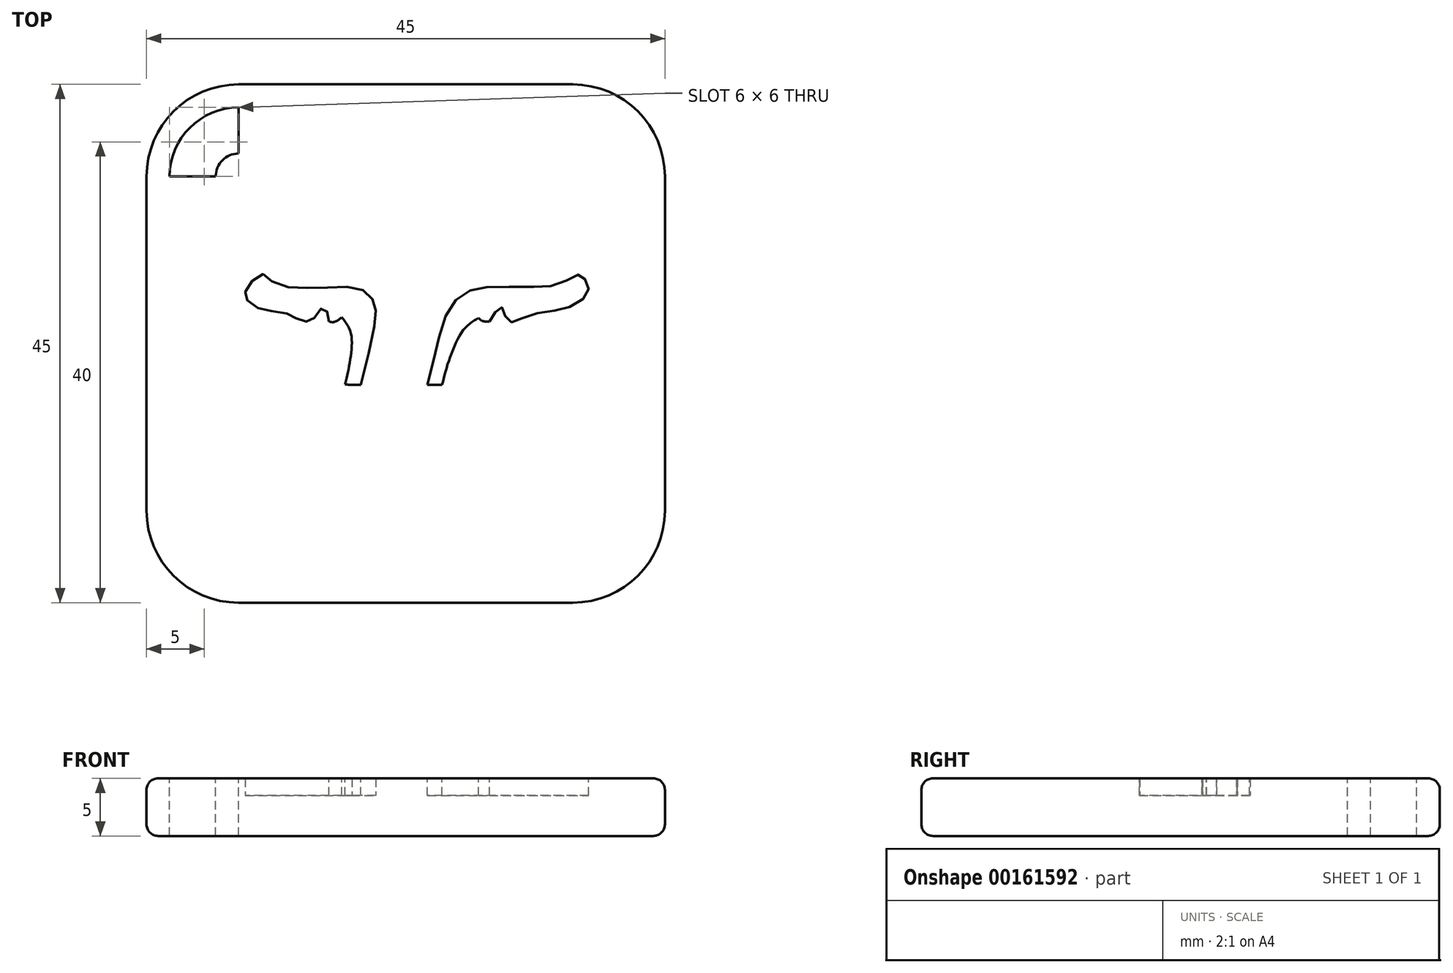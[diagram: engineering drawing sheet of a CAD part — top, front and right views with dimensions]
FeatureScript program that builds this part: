
annotation { "Feature Type Name" : "Feature", "Feature Type Description" : "" }
export const myFeature = defineFeature(function(context is Context, id is Id, definition is map)
    precondition{}
    {
        {
            var Q0;
            Q0=qCreatedBy(makeId("Top.planeOp"),FACE);
            var sketch = newSketch(context, id + "F0", { "sketchPlane" : qUnion([Q0])});
            skLineSegment(sketch, "E0.bottom", {"start": v(-22.5, 22.5) * mm, "end": v(22.5, 22.5) * mm});
            skLineSegment(sketch, "E0.top", {"start": v(-22.5, -22.5) * mm, "end": v(22.5, -22.5) * mm});
            skLineSegment(sketch, "E0.left", {"start": v(-22.5, 22.5) * mm, "end": v(-22.5, -22.5) * mm});
            skLineSegment(sketch, "E0.right", {"start": v(22.5, 22.5) * mm, "end": v(22.5, -22.5) * mm});
            skPoint(sketch, "E1", {"position": v(0, 22.5) * mm});
            skPoint(sketch, "E2", {"position": v(22.5, 0) * mm});
            skSolve(sketch);
        }
        {
            var Q0;
            Q0=qSketchRegion(id+"F0",true);
            extrude(context, id + "F1", {"entities" : qUnion([Q0]), "depth" : 5 * mm});
        }
        {
            var Q0;
            Q0=makeQuery(id+"F1.opExtrude","CAP_FACE",FACE,{"disambiguationData":[OSD([sQuery(id+"F0.wireOp",EDGE,"E0.bottom"),sQuery(id+"F0.wireOp",EDGE,"E0.top"),sQuery(id+"F0.wireOp",EDGE,"E0.left"),sQuery(id+"F0.wireOp",EDGE,"E0.right")])],"isStart":false});
            var sketch = newSketch(context, id + "F2", { "sketchPlane" : qUnion([Q0])});
            skPoint(sketch, "E3", {"position": v(0, 19.42) * mm});
            skPoint(sketch, "E4", {"position": v(22.5, 0) * mm});
            skPoint(sketch, "E5", {"position": v(0, 22.5) * mm});
            skFitSpline(sketch, "E6", {"points": [v(-10.99, 17.96) * mm, v(-6.67, 16.95) * mm, v(-3.8, 15.5) * mm, v(-1.73, 13.83) * mm], "startDerivative": vector(12.1, -2.63) * mm, "endDerivative": vector(7.1, -5.95) * mm});
            skFitSpline(sketch, "E7", {"points": [v(-1.73, 13.83) * mm, v(1.93, 14.01) * mm, v(5.49, 13.96) * mm, v(8.15, 13.83) * mm], "startDerivative": vector(10.33, 0.9) * mm, "endDerivative": vector(8.55, -0.72) * mm});
            skFitSpline(sketch, "E8", {"points": [v(8.15, 13.83) * mm, v(9.82, 14.8) * mm, v(13.73, 16.7) * mm, v(19.48, 18.03) * mm], "startDerivative": vector(6.27, 4) * mm, "endDerivative": vector(14.4, 2.4) * mm});
            skFitSpline(sketch, "E9", {"points": [v(19.48, 18.03) * mm, v(19.95, 16.98) * mm, v(20.58, 14.3) * mm, v(20.04, 11.7) * mm, v(19.14, 9.8) * mm, v(17.57, 7.66) * mm, v(17.57, 7.66) * mm], "startDerivative": vector(3.43, -6.2) * mm, "endDerivative": vector(-0.62, 0.45) * mm});
            skFitSpline(sketch, "E10", {"points": [v(17.57, 7.66) * mm, v(18.66, 6.83) * mm, v(19.79, 5.6) * mm, v(21, 3.47) * mm, v(21.02, 1.64) * mm, v(20.45, -0.51) * mm, v(19.02, -3.1) * mm], "startDerivative": vector(7.54, -6.14) * mm, "endDerivative": vector(-8.05, -12.97) * mm});
            skFitSpline(sketch, "E11", {"points": [v(19.02, -3.1) * mm, v(18.46, -2.57) * mm, v(17.94, -2.35) * mm], "startDerivative": vector(-1.02, 1.1) * mm, "endDerivative": vector(-1.13, 0.4) * mm});
            skFitSpline(sketch, "E12", {"points": [v(17.94, -2.35) * mm, v(17.32, -3.93) * mm, v(16.2, -5.3) * mm, v(15.51, -5.8) * mm], "startDerivative": vector(-1.51, -4.58) * mm, "endDerivative": vector(-1.47, -1.77) * mm});
            skFitSpline(sketch, "E13", {"points": [v(15.51, -5.8) * mm, v(15.34, -4.95) * mm, v(14.8, -4.37) * mm], "startDerivative": vector(-0.01, 1.8) * mm, "endDerivative": vector(-0.19, 0.23) * mm});
            skFitSpline(sketch, "E14", {"points": [v(14.8, -4.37) * mm, v(14.55, -4.88) * mm, v(13.51, -6.28) * mm, v(12.21, -7.43) * mm, v(11.26, -7.78) * mm], "startDerivative": vector(-1.12, -2.62) * mm, "endDerivative": vector(-4.09, -1.1) * mm});
            skFitSpline(sketch, "E15", {"points": [v(11.26, -7.78) * mm, v(11.11, -6.74) * mm, v(10.42, -5.88) * mm], "startDerivative": vector(-0.05, 2.2) * mm, "endDerivative": vector(-1.63, 1.67) * mm});
            skFitSpline(sketch, "E16", {"points": [v(10.42, -5.88) * mm, v(10.03, -6.36) * mm, v(8.14, -8.14) * mm, v(6.66, -8.75) * mm], "startDerivative": vector(-1.32, -1.92) * mm, "endDerivative": vector(-4.03, -1) * mm});
            skFitSpline(sketch, "E17", {"points": [v(6.66, -8.75) * mm, v(6.66, -7.96) * mm, v(6.49, -7.01) * mm, v(6.05, -6.24) * mm, v(5.88, -6.12) * mm], "startDerivative": vector(0.1, 2.83) * mm, "endDerivative": vector(-1.15, 0.55) * mm});
            skFitSpline(sketch, "E18", {"points": [v(5.88, -6.12) * mm, v(5.27, -6.68) * mm, v(2.3, -11.05) * mm, v(-0.84, -15.23) * mm, v(-3.18, -17.45) * mm, v(-4.52, -17.94) * mm, v(-5.68, -17.34) * mm, v(-6.99, -14.65) * mm, v(-8.74, -7.01) * mm, v(-9.06, -6.15) * mm], "startDerivative": vector(-8.59, -6.54) * mm, "endDerivative": vector(-4.62, 9.1) * mm});
            skFitSpline(sketch, "E19", {"points": [v(-9.06, -6.15) * mm, v(-9.62, -6.41) * mm, v(-10.7, -7.74) * mm, v(-11.17, -8.83) * mm], "startDerivative": vector(-2.18, -0.85) * mm, "endDerivative": vector(-0.22, -0.54) * mm});
            skFitSpline(sketch, "E20", {"points": [v(-11.17, -8.83) * mm, v(-11.66, -8.51) * mm, v(-12.52, -7.94) * mm, v(-13.28, -6.72) * mm, v(-13.5, -5.86) * mm], "startDerivative": vector(-2.33, 1.17) * mm, "endDerivative": vector(-0.64, 3.34) * mm});
            skFitSpline(sketch, "E21", {"points": [v(-13.5, -5.86) * mm, v(-14.15, -6.26) * mm, v(-15.03, -7.37) * mm, v(-15.3, -7.76) * mm], "startDerivative": vector(-1.95, -0.91) * mm, "endDerivative": vector(-0.85, -1.3) * mm});
            skFitSpline(sketch, "E22", {"points": [v(-15.3, -7.76) * mm, v(-15.84, -7.58) * mm, v(-16.47, -7.03) * mm, v(-16.9, -6.04) * mm, v(-17.12, -5.3) * mm, v(-17.21, -4.47) * mm], "startDerivative": vector(-3.23, 0.77) * mm, "endDerivative": vector(-0.32, 4.26) * mm});
            skFitSpline(sketch, "E23", {"points": [v(-17.21, -4.47) * mm, v(-17.79, -4.83) * mm, v(-18.39, -5.5) * mm, v(-18.57, -5.76) * mm], "startDerivative": vector(-1.6, -0.83) * mm, "endDerivative": vector(-0.61, -0.95) * mm});
            skFitSpline(sketch, "E24", {"points": [v(-18.57, -5.76) * mm, v(-18.91, -5.4) * mm, v(-19.37, -4.63) * mm, v(-19.48, -3.72) * mm, v(-19.42, -2.9) * mm, v(-19.34, -2.33) * mm], "startDerivative": vector(-1.95, 2) * mm, "endDerivative": vector(0.47, 3.1) * mm});
            skFitSpline(sketch, "E25", {"points": [v(-19.34, -2.33) * mm, v(-19.79, -2.53) * mm, v(-20.83, -3) * mm], "startDerivative": vector(-1.04, -0.42) * mm, "endDerivative": vector(-1.81, -1.1) * mm});
            skFitSpline(sketch, "E26", {"points": [v(-20.83, -3) * mm, v(-21, -1.25) * mm, v(-19.6, 3.43) * mm, v(-14.29, 7.66) * mm], "startDerivative": vector(-1.5, 7.35) * mm, "endDerivative": vector(14.98, 8.8) * mm});
            skFitSpline(sketch, "E27", {"points": [v(-14.29, 7.66) * mm, v(-14.63, 9.8) * mm, v(-14.46, 12.44) * mm, v(-13.34, 15.3) * mm, v(-10.99, 17.96) * mm], "startDerivative": vector(-2.7, 9.33) * mm, "endDerivative": vector(8.61, 9.84) * mm});
            skFitSpline(sketch, "E28", {"points": [v(-11.82, 7.22) * mm, v(-12.36, 11.13) * mm, v(-11.43, 14.91) * mm, v(-10.34, 16.17) * mm], "startDerivative": vector(-2.56, 9.75) * mm, "endDerivative": vector(4.88, 4.44) * mm});
            skFitSpline(sketch, "E29", {"points": [v(-10.34, 16.17) * mm, v(-6.96, 15.19) * mm, v(-4.57, 13.4) * mm, v(-2.66, 11.86) * mm], "startDerivative": vector(9.47, -2.48) * mm, "endDerivative": vector(5.95, -4.79) * mm});
            skFitSpline(sketch, "E30", {"points": [v(-2.66, 11.86) * mm, v(-0.71, 12) * mm, v(1.24, 12.12) * mm, v(5.72, 12.04) * mm, v(8.17, 11.86) * mm], "startDerivative": vector(9.3, 1.33) * mm, "endDerivative": vector(8.98, -1.39) * mm});
            skFitSpline(sketch, "E31", {"points": [v(8.17, 11.86) * mm, v(11.95, 14.03) * mm, v(16.86, 16.09) * mm, v(17.95, 16.22) * mm], "startDerivative": vector(9.23, 6) * mm, "endDerivative": vector(5.74, 0.8) * mm});
            skFitSpline(sketch, "E32", {"points": [v(17.95, 16.22) * mm, v(18.34, 15.3) * mm, v(18.46, 13.86) * mm, v(17.71, 11.66) * mm, v(15.1, 7.33) * mm], "startDerivative": vector(2.53, -5.22) * mm, "endDerivative": vector(-7.95, -12.35) * mm});
            skFitSpline(sketch, "E33", {"points": [v(15.1, 7.33) * mm, v(16.28, 6.28) * mm, v(17.98, 4.2) * mm, v(18.58, 1.32) * mm, v(18.17, -0.47) * mm], "startDerivative": vector(5.27, -4.55) * mm, "endDerivative": vector(-2.46, -7.24) * mm});
            skFitSpline(sketch, "E34", {"points": [v(18.17, -0.47) * mm, v(16.95, -0.28) * mm, v(15.74, -2.26) * mm], "startDerivative": vector(-3.13, 1.27) * mm, "endDerivative": vector(-1.85, -4.58) * mm});
            skFitSpline(sketch, "E35", {"points": [v(15.74, -2.26) * mm, v(14.32, -2.15) * mm, v(13.59, -2.49) * mm, v(12.9, -3.53) * mm, v(12.5, -4.63) * mm], "startDerivative": vector(-5.57, 0.88) * mm, "endDerivative": vector(-1.39, -4.3) * mm});
            skFitSpline(sketch, "E36", {"points": [v(12.5, -4.63) * mm, v(11.93, -3.83) * mm, v(10.85, -3.58) * mm, v(9.81, -4.1) * mm, v(8.35, -5.47) * mm], "startDerivative": vector(-2.05, 4.14) * mm, "endDerivative": vector(-4.82, -4.89) * mm});
            skFitSpline(sketch, "E37", {"points": [v(8.35, -5.47) * mm, v(7.95, -4.7) * mm, v(7.25, -3.94) * mm, v(6.42, -3.66) * mm, v(5.29, -3.83) * mm, v(4, -4.56) * mm, v(3.16, -5.88) * mm, v(1.27, -8.94) * mm, v(-1.32, -12.8) * mm, v(-3.03, -15.03) * mm, v(-3.77, -15.73) * mm, v(-3.98, -15.77) * mm, v(-4.3, -15.47) * mm, v(-4.8, -13.94) * mm, v(-5.58, -10.32) * mm, v(-6.04, -7.02) * mm, v(-6.35, -4.77) * mm, v(-6.82, -4.04) * mm, v(-7.86, -3.7) * mm, v(-8.72, -3.71) * mm, v(-9.28, -3.93) * mm, v(-10.11, -4.4) * mm, v(-11.18, -5.47) * mm], "startDerivative": vector(-10.14, 22.02) * mm, "endDerivative": vector(-23.4, -25.47) * mm});
            skFitSpline(sketch, "E38", {"points": [v(-11.18, -5.47) * mm, v(-11.68, -4.42) * mm, v(-12.64, -3.6) * mm, v(-13.9, -3.83) * mm, v(-15.05, -4.75) * mm], "startDerivative": vector(-1.65, 4.4) * mm, "endDerivative": vector(-3.87, -3.5) * mm});
            skFitSpline(sketch, "E39", {"points": [v(-15.05, -4.75) * mm, v(-14.87, -3.44) * mm, v(-15.11, -2.36) * mm, v(-16.79, -2.2) * mm, v(-17.15, -2.32) * mm], "startDerivative": vector(0.33, 4.33) * mm, "endDerivative": vector(-1.67, -0.76) * mm});
            skFitSpline(sketch, "E40", {"points": [v(-17.15, -2.32) * mm, v(-17.1, -1.32) * mm, v(-17.21, -0.43) * mm, v(-18.6, -0.43) * mm], "startDerivative": vector(0.04, 3) * mm, "endDerivative": vector(-4.65, -0.92) * mm});
            skFitSpline(sketch, "E41", {"points": [v(-18.6, -0.43) * mm, v(-17.48, 2.56) * mm, v(-14.24, 5.72) * mm, v(-11.82, 7.22) * mm], "startDerivative": vector(2.26, 9.56) * mm, "endDerivative": vector(7.62, 4.87) * mm});
            skFitSpline(sketch, "E42", {"points": [v(-3.9, -3.58) * mm, v(-5.25, -3.56) * mm], "startDerivative": vector(-2.2, -0.06) * mm, "endDerivative": vector(-0.4, -0.03) * mm});
            skFitSpline(sketch, "E43", {"points": [v(-5.25, -3.56) * mm, v(-4.8, -1.32) * mm, v(-4.78, 0.95) * mm, v(-5.54, 2.28) * mm], "startDerivative": vector(1.38, 6.15) * mm, "endDerivative": vector(-3.2, 4.1) * mm});
            skFitSpline(sketch, "E44", {"points": [v(-5.54, 2.28) * mm, v(-6.24, 1.87) * mm, v(-6.65, 1.91) * mm], "startDerivative": vector(-1.27, -0.93) * mm, "endDerivative": vector(-0.93, 0.27) * mm});
            skFitSpline(sketch, "E45", {"points": [v(-6.65, 1.91) * mm, v(-6.77, 2.6) * mm, v(-7, 3.06) * mm, v(-7.38, 3) * mm, v(-7.9, 2.25) * mm, v(-8.3, 1.95) * mm, v(-8.98, 1.95) * mm, v(-9.73, 2.32) * mm, v(-10.35, 2.61) * mm, v(-12.05, 2.87) * mm, v(-13.04, 3.2) * mm, v(-13.83, 3.89) * mm, v(-13.94, 4.34) * mm, v(-13.7, 5) * mm, v(-12.5, 6.03) * mm, v(-12.24, 5.91) * mm, v(-11.08, 5.11) * mm, v(-8.85, 4.83) * mm, v(-6.2, 4.9) * mm, v(-4.05, 4.8) * mm, v(-3, 4.05) * mm, v(-2.64, 3.17) * mm, v(-2.67, 1.87) * mm, v(-3.9, -3.58) * mm], "startDerivative": vector(-3.06, 20.2) * mm, "endDerivative": vector(-16.31, -66) * mm});
            skFitSpline(sketch, "E46", {"points": [v(1.89, -3.57) * mm, v(3.16, -3.59) * mm], "startDerivative": vector(1.31, -0.04) * mm, "endDerivative": vector(1.31, -0.04) * mm});
            skFitSpline(sketch, "E47", {"points": [v(3.16, -3.59) * mm, v(3.87, -1.13) * mm, v(5.14, 1.33) * mm, v(6.31, 2.22) * mm], "startDerivative": vector(1.57, 6.66) * mm, "endDerivative": vector(4.3, 2.6) * mm});
            skFitSpline(sketch, "E48", {"points": [v(6.31, 2.22) * mm, v(6.7, 1.95) * mm, v(7.26, 1.91) * mm], "startDerivative": vector(0.78, -0.73) * mm, "endDerivative": vector(0.04, 0) * mm});
            skFitSpline(sketch, "E49", {"points": [v(7.26, 1.91) * mm, v(7.72, 2.67) * mm, v(8.08, 3.08) * mm, v(8.43, 3.1) * mm, v(8.62, 2.43) * mm, v(8.96, 1.92) * mm, v(9.55, 1.92) * mm, v(10.74, 2.48) * mm, v(12.79, 2.84) * mm, v(14.39, 3.25) * mm, v(15.67, 4.16) * mm, v(15.87, 4.85) * mm, v(15.6, 5.54) * mm, v(15.11, 5.98) * mm, v(14.78, 5.9) * mm, v(13.15, 5.13) * mm, v(11.5, 4.91) * mm, v(7.66, 4.9) * mm, v(5.54, 4.58) * mm, v(3.92, 3.28) * mm, v(2.87, 0.42) * mm, v(1.89, -3.57) * mm], "startDerivative": vector(12.23, 20.39) * mm, "endDerivative": vector(-12.15, -48.42) * mm});
            skSolve(sketch);
        }
        {
            var Q0;
            Q0=makeQuery(id+"F2.imprint","IMPRINT",FACE,{"disambiguationData":[TD([[makeQuery(id+"F2.imprint","IMPRINT",EDGE,{"derivedFrom":sQuery(id+"F2.wireOp",EDGE,"E6")}),-1.0]])]});
            var Q1;
            Q1=makeQuery(id+"F2.imprint","IMPRINT",FACE,{"disambiguationData":[TD([[makeQuery(id+"F2.imprint","IMPRINT",EDGE,{"derivedFrom":sQuery(id+"F2.wireOp",EDGE,"E42")}),-1.0]])]});
            var Q2;
            Q2=makeQuery(id+"F2.imprint","IMPRINT",FACE,{"disambiguationData":[TD([[makeQuery(id+"F2.imprint","IMPRINT",EDGE,{"derivedFrom":sQuery(id+"F2.wireOp",EDGE,"E46")}),1.0]])]});
            extrude(context, id + "F3", {"entities" : qUnion([Q0, Q1, Q2]), "operationType" : NewBodyOperationType.REMOVE, "oppositeDirection" : true, "depth" : 1.5 * mm});
        }
        {
            var Q0;
            Q0=makeQuery(id+"F1.opExtrude","SWEPT_EDGE",EDGE,{"disambiguationData":[OSD([sQuery(id+"F0.wireOp",EDGE,"E0.top"),sQuery(id+"F0.wireOp",EDGE,"E0.right")])]});
            var Q1;
            Q1=makeQuery(id+"F1.opExtrude","SWEPT_EDGE",EDGE,{"disambiguationData":[OSD([sQuery(id+"F0.wireOp",EDGE,"E0.top"),sQuery(id+"F0.wireOp",EDGE,"E0.left")])]});
            var Q2;
            Q2=makeQuery(id+"F1.opExtrude","SWEPT_EDGE",EDGE,{"disambiguationData":[OSD([sQuery(id+"F0.wireOp",EDGE,"E0.bottom"),sQuery(id+"F0.wireOp",EDGE,"E0.left")])]});
            var Q3;
            Q3=makeQuery(id+"F1.opExtrude","SWEPT_EDGE",EDGE,{"disambiguationData":[OSD([sQuery(id+"F0.wireOp",EDGE,"E0.bottom"),sQuery(id+"F0.wireOp",EDGE,"E0.right")])]});
            fillet(context, id + "F4", {"entities" : qUnion([Q0, Q1, Q2, Q3]), "radius" : 8 * mm, "tangentPropagation" : true, "allowEdgeOverflow" : false});
        }
        {
            var Q0;
            {var subQ0=sQuery(id+"F0.wireOp",EDGE,"E0.left");var subQ1=sQuery(id+"F0.wireOp",EDGE,"E0.bottom");var subQ2=sQuery(id+"F0.wireOp",EDGE,"E0.right");var subQ3=sQuery(id+"F0.wireOp",EDGE,"E0.top");Q0=makeQuery(id+"F3.boolean.opBoolean","SPLIT",FACE,{"disambiguationData":[TD([makeQuery(id+"F1.opExtrude","SWEPT_FACE",FACE,{"disambiguationData":[OSD([subQ1])]})])],"derivedFrom":makeQuery(id+"F1.opExtrude","CAP_FACE",FACE,{"disambiguationData":[OSD([subQ1,subQ3,subQ0,subQ2])],"isStart":false})});}
            var sketch = newSketch(context, id + "F5", { "sketchPlane" : qUnion([Q0])});
            skArc(sketch, "E50", {"start": v(-14.5, 22.5) * mm, "mid": v(-20.16, 20.16) * mm, "end": v(-22.5, 14.5) * mm});
            skArc(sketch, "E51.0", {"start": v(-14.5, 20.5) * mm, "mid": v(-18.74, 18.74) * mm, "end": v(-20.5, 14.5) * mm});
            skArc(sketch, "E52.0", {"start": v(-14.5, 16.5) * mm, "mid": v(-15.91, 15.91) * mm, "end": v(-16.5, 14.5) * mm});
            skLineSegment(sketch, "E53", {"start": v(-14.5, 16.5) * mm, "end": v(-14.5, 20.5) * mm});
            skLineSegment(sketch, "E54", {"start": v(-16.5, 14.5) * mm, "end": v(-20.5, 14.5) * mm});
            skSolve(sketch);
        }
        {
            var Q0;
            Q0 = qSketchRegion(id + "F5", true);
            var Q1;
            Q1=makeQuery(id+"F1.opExtrude","CAP_FACE",FACE,{"disambiguationData":[OSD([sQuery(id+"F0.wireOp",EDGE,"E0.bottom"),sQuery(id+"F0.wireOp",EDGE,"E0.top"),sQuery(id+"F0.wireOp",EDGE,"E0.left"),sQuery(id+"F0.wireOp",EDGE,"E0.right")])],"isStart":true});
            extrude(context, id + "F6", {"entities" : qUnion([Q0]), "operationType" : NewBodyOperationType.REMOVE, "endBound" : BoundingType.UP_TO_SURFACE, "oppositeDirection" : true, "endBoundEntityFace" : qUnion([Q1]), "depth" : 25 * mm});
        }
        {
            var Q0;
            Q0=makeQuery(id+"F1.opExtrude","CAP_EDGE",EDGE,{"disambiguationData":[OSD([sQuery(id+"F0.wireOp",EDGE,"E0.top")])],"isStart":false});
            var Q1;
            {var subQ0=sQuery(id+"F0.wireOp",EDGE,"E0.left");var subQ1=sQuery(id+"F0.wireOp",EDGE,"E0.bottom");var subQ2=sQuery(id+"F0.wireOp",EDGE,"E0.right");var subQ3=sQuery(id+"F0.wireOp",EDGE,"E0.top");Q1=makeQuery(id+"F4.opFillet","BLEND_EDGE",EDGE,{"blendedFrom":[makeQuery(id+"F1.opExtrude","SWEPT_EDGE",EDGE,{"disambiguationData":[OSD([subQ3,subQ2])]}),makeQuery(id+"F3.boolean.opBoolean","SPLIT",FACE,{"disambiguationData":[TD([makeQuery(id+"F1.opExtrude","SWEPT_FACE",FACE,{"disambiguationData":[OSD([subQ1])]})])],"derivedFrom":makeQuery(id+"F1.opExtrude","CAP_FACE",FACE,{"disambiguationData":[OSD([subQ1,subQ3,subQ0,subQ2])],"isStart":false})})],"blendedInto":[makeQuery(id+"F3.boolean.opBoolean","SPLIT",FACE,{"disambiguationData":[TD([makeQuery(id+"F1.opExtrude","SWEPT_FACE",FACE,{"disambiguationData":[OSD([subQ1])]})])],"derivedFrom":makeQuery(id+"F1.opExtrude","CAP_FACE",FACE,{"disambiguationData":[OSD([subQ1,subQ3,subQ0,subQ2])],"isStart":false})})]});}
            var Q2;
            Q2=makeQuery(id+"F1.opExtrude","CAP_EDGE",EDGE,{"disambiguationData":[OSD([sQuery(id+"F0.wireOp",EDGE,"E0.right")])],"isStart":false});
            var Q3;
            {var subQ0=sQuery(id+"F0.wireOp",EDGE,"E0.left");var subQ1=sQuery(id+"F0.wireOp",EDGE,"E0.bottom");var subQ2=sQuery(id+"F0.wireOp",EDGE,"E0.right");var subQ3=sQuery(id+"F0.wireOp",EDGE,"E0.top");Q3=makeQuery(id+"F4.opFillet","BLEND_EDGE",EDGE,{"blendedFrom":[makeQuery(id+"F1.opExtrude","SWEPT_EDGE",EDGE,{"disambiguationData":[OSD([subQ1,subQ2])]}),makeQuery(id+"F3.boolean.opBoolean","SPLIT",FACE,{"disambiguationData":[TD([makeQuery(id+"F1.opExtrude","SWEPT_FACE",FACE,{"disambiguationData":[OSD([subQ1])]})])],"derivedFrom":makeQuery(id+"F1.opExtrude","CAP_FACE",FACE,{"disambiguationData":[OSD([subQ1,subQ3,subQ0,subQ2])],"isStart":false})})],"blendedInto":[makeQuery(id+"F3.boolean.opBoolean","SPLIT",FACE,{"disambiguationData":[TD([makeQuery(id+"F1.opExtrude","SWEPT_FACE",FACE,{"disambiguationData":[OSD([subQ1])]})])],"derivedFrom":makeQuery(id+"F1.opExtrude","CAP_FACE",FACE,{"disambiguationData":[OSD([subQ1,subQ3,subQ0,subQ2])],"isStart":false})})]});}
            var Q4;
            Q4=makeQuery(id+"F1.opExtrude","CAP_EDGE",EDGE,{"disambiguationData":[OSD([sQuery(id+"F0.wireOp",EDGE,"E0.bottom")])],"isStart":false});
            var Q5;
            {var subQ0=sQuery(id+"F0.wireOp",EDGE,"E0.left");var subQ1=sQuery(id+"F0.wireOp",EDGE,"E0.bottom");var subQ2=sQuery(id+"F0.wireOp",EDGE,"E0.right");var subQ3=sQuery(id+"F0.wireOp",EDGE,"E0.top");Q5=makeQuery(id+"F4.opFillet","BLEND_EDGE",EDGE,{"blendedFrom":[makeQuery(id+"F1.opExtrude","SWEPT_EDGE",EDGE,{"disambiguationData":[OSD([subQ1,subQ0])]}),makeQuery(id+"F3.boolean.opBoolean","SPLIT",FACE,{"disambiguationData":[TD([makeQuery(id+"F1.opExtrude","SWEPT_FACE",FACE,{"disambiguationData":[OSD([subQ1])]})])],"derivedFrom":makeQuery(id+"F1.opExtrude","CAP_FACE",FACE,{"disambiguationData":[OSD([subQ1,subQ3,subQ0,subQ2])],"isStart":false})})],"blendedInto":[makeQuery(id+"F3.boolean.opBoolean","SPLIT",FACE,{"disambiguationData":[TD([makeQuery(id+"F1.opExtrude","SWEPT_FACE",FACE,{"disambiguationData":[OSD([subQ1])]})])],"derivedFrom":makeQuery(id+"F1.opExtrude","CAP_FACE",FACE,{"disambiguationData":[OSD([subQ1,subQ3,subQ0,subQ2])],"isStart":false})})]});}
            var Q6;
            Q6=makeQuery(id+"F1.opExtrude","CAP_EDGE",EDGE,{"disambiguationData":[OSD([sQuery(id+"F0.wireOp",EDGE,"E0.left")])],"isStart":false});
            var Q7;
            {var subQ0=sQuery(id+"F0.wireOp",EDGE,"E0.left");var subQ1=sQuery(id+"F0.wireOp",EDGE,"E0.bottom");var subQ2=sQuery(id+"F0.wireOp",EDGE,"E0.right");var subQ3=sQuery(id+"F0.wireOp",EDGE,"E0.top");Q7=makeQuery(id+"F4.opFillet","BLEND_EDGE",EDGE,{"blendedFrom":[makeQuery(id+"F1.opExtrude","SWEPT_EDGE",EDGE,{"disambiguationData":[OSD([subQ3,subQ0])]}),makeQuery(id+"F3.boolean.opBoolean","SPLIT",FACE,{"disambiguationData":[TD([makeQuery(id+"F1.opExtrude","SWEPT_FACE",FACE,{"disambiguationData":[OSD([subQ1])]})])],"derivedFrom":makeQuery(id+"F1.opExtrude","CAP_FACE",FACE,{"disambiguationData":[OSD([subQ1,subQ3,subQ0,subQ2])],"isStart":false})})],"blendedInto":[makeQuery(id+"F3.boolean.opBoolean","SPLIT",FACE,{"disambiguationData":[TD([makeQuery(id+"F1.opExtrude","SWEPT_FACE",FACE,{"disambiguationData":[OSD([subQ1])]})])],"derivedFrom":makeQuery(id+"F1.opExtrude","CAP_FACE",FACE,{"disambiguationData":[OSD([subQ1,subQ3,subQ0,subQ2])],"isStart":false})})]});}
            fillet(context, id + "F7", {"entities" : qUnion([Q0, Q1, Q2, Q3, Q4, Q5, Q6, Q7]), "radius" : 1 * mm, "tangentPropagation" : true, "allowEdgeOverflow" : false});
        }
        {
            var Q0;
            Q0=makeQuery(id+"F1.opExtrude","CAP_EDGE",EDGE,{"disambiguationData":[OSD([sQuery(id+"F0.wireOp",EDGE,"E0.top")])],"isStart":true});
            var Q1;
            {var subQ0=sQuery(id+"F0.wireOp",EDGE,"E0.left");var subQ1=sQuery(id+"F0.wireOp",EDGE,"E0.top");Q1=makeQuery(id+"F4.opFillet","BLEND_EDGE",EDGE,{"blendedFrom":[makeQuery(id+"F1.opExtrude","SWEPT_EDGE",EDGE,{"disambiguationData":[OSD([subQ1,subQ0])]}),makeQuery(id+"F1.opExtrude","CAP_FACE",FACE,{"disambiguationData":[OSD([sQuery(id+"F0.wireOp",EDGE,"E0.bottom"),subQ1,subQ0,sQuery(id+"F0.wireOp",EDGE,"E0.right")])],"isStart":true})],"blendedInto":[makeQuery(id+"F1.opExtrude","CAP_FACE",FACE,{"disambiguationData":[OSD([sQuery(id+"F0.wireOp",EDGE,"E0.bottom"),subQ1,subQ0,sQuery(id+"F0.wireOp",EDGE,"E0.right")])],"isStart":true})]});}
            var Q2;
            Q2=makeQuery(id+"F1.opExtrude","CAP_EDGE",EDGE,{"disambiguationData":[OSD([sQuery(id+"F0.wireOp",EDGE,"E0.left")])],"isStart":true});
            var Q3;
            {var subQ0=sQuery(id+"F0.wireOp",EDGE,"E0.left");var subQ1=sQuery(id+"F0.wireOp",EDGE,"E0.bottom");Q3=makeQuery(id+"F4.opFillet","BLEND_EDGE",EDGE,{"blendedFrom":[makeQuery(id+"F1.opExtrude","SWEPT_EDGE",EDGE,{"disambiguationData":[OSD([subQ1,subQ0])]}),makeQuery(id+"F1.opExtrude","CAP_FACE",FACE,{"disambiguationData":[OSD([subQ1,sQuery(id+"F0.wireOp",EDGE,"E0.top"),subQ0,sQuery(id+"F0.wireOp",EDGE,"E0.right")])],"isStart":true})],"blendedInto":[makeQuery(id+"F1.opExtrude","CAP_FACE",FACE,{"disambiguationData":[OSD([subQ1,sQuery(id+"F0.wireOp",EDGE,"E0.top"),subQ0,sQuery(id+"F0.wireOp",EDGE,"E0.right")])],"isStart":true})]});}
            var Q4;
            Q4=makeQuery(id+"F1.opExtrude","CAP_EDGE",EDGE,{"disambiguationData":[OSD([sQuery(id+"F0.wireOp",EDGE,"E0.bottom")])],"isStart":true});
            var Q5;
            {var subQ0=sQuery(id+"F0.wireOp",EDGE,"E0.right");var subQ1=sQuery(id+"F0.wireOp",EDGE,"E0.bottom");Q5=makeQuery(id+"F4.opFillet","BLEND_EDGE",EDGE,{"blendedFrom":[makeQuery(id+"F1.opExtrude","SWEPT_EDGE",EDGE,{"disambiguationData":[OSD([subQ1,subQ0])]}),makeQuery(id+"F1.opExtrude","CAP_FACE",FACE,{"disambiguationData":[OSD([subQ1,sQuery(id+"F0.wireOp",EDGE,"E0.top"),sQuery(id+"F0.wireOp",EDGE,"E0.left"),subQ0])],"isStart":true})],"blendedInto":[makeQuery(id+"F1.opExtrude","CAP_FACE",FACE,{"disambiguationData":[OSD([subQ1,sQuery(id+"F0.wireOp",EDGE,"E0.top"),sQuery(id+"F0.wireOp",EDGE,"E0.left"),subQ0])],"isStart":true})]});}
            var Q6;
            Q6=makeQuery(id+"F1.opExtrude","CAP_EDGE",EDGE,{"disambiguationData":[OSD([sQuery(id+"F0.wireOp",EDGE,"E0.right")])],"isStart":true});
            var Q7;
            {var subQ0=sQuery(id+"F0.wireOp",EDGE,"E0.right");var subQ1=sQuery(id+"F0.wireOp",EDGE,"E0.top");Q7=makeQuery(id+"F4.opFillet","BLEND_EDGE",EDGE,{"blendedFrom":[makeQuery(id+"F1.opExtrude","SWEPT_EDGE",EDGE,{"disambiguationData":[OSD([subQ1,subQ0])]}),makeQuery(id+"F1.opExtrude","CAP_FACE",FACE,{"disambiguationData":[OSD([sQuery(id+"F0.wireOp",EDGE,"E0.bottom"),subQ1,sQuery(id+"F0.wireOp",EDGE,"E0.left"),subQ0])],"isStart":true})],"blendedInto":[makeQuery(id+"F1.opExtrude","CAP_FACE",FACE,{"disambiguationData":[OSD([sQuery(id+"F0.wireOp",EDGE,"E0.bottom"),subQ1,sQuery(id+"F0.wireOp",EDGE,"E0.left"),subQ0])],"isStart":true})]});}
            fillet(context, id + "F8", {"entities" : qUnion([Q0, Q1, Q2, Q3, Q4, Q5, Q6, Q7]), "radius" : 1 * mm, "tangentPropagation" : true, "allowEdgeOverflow" : false});
        }
    });
